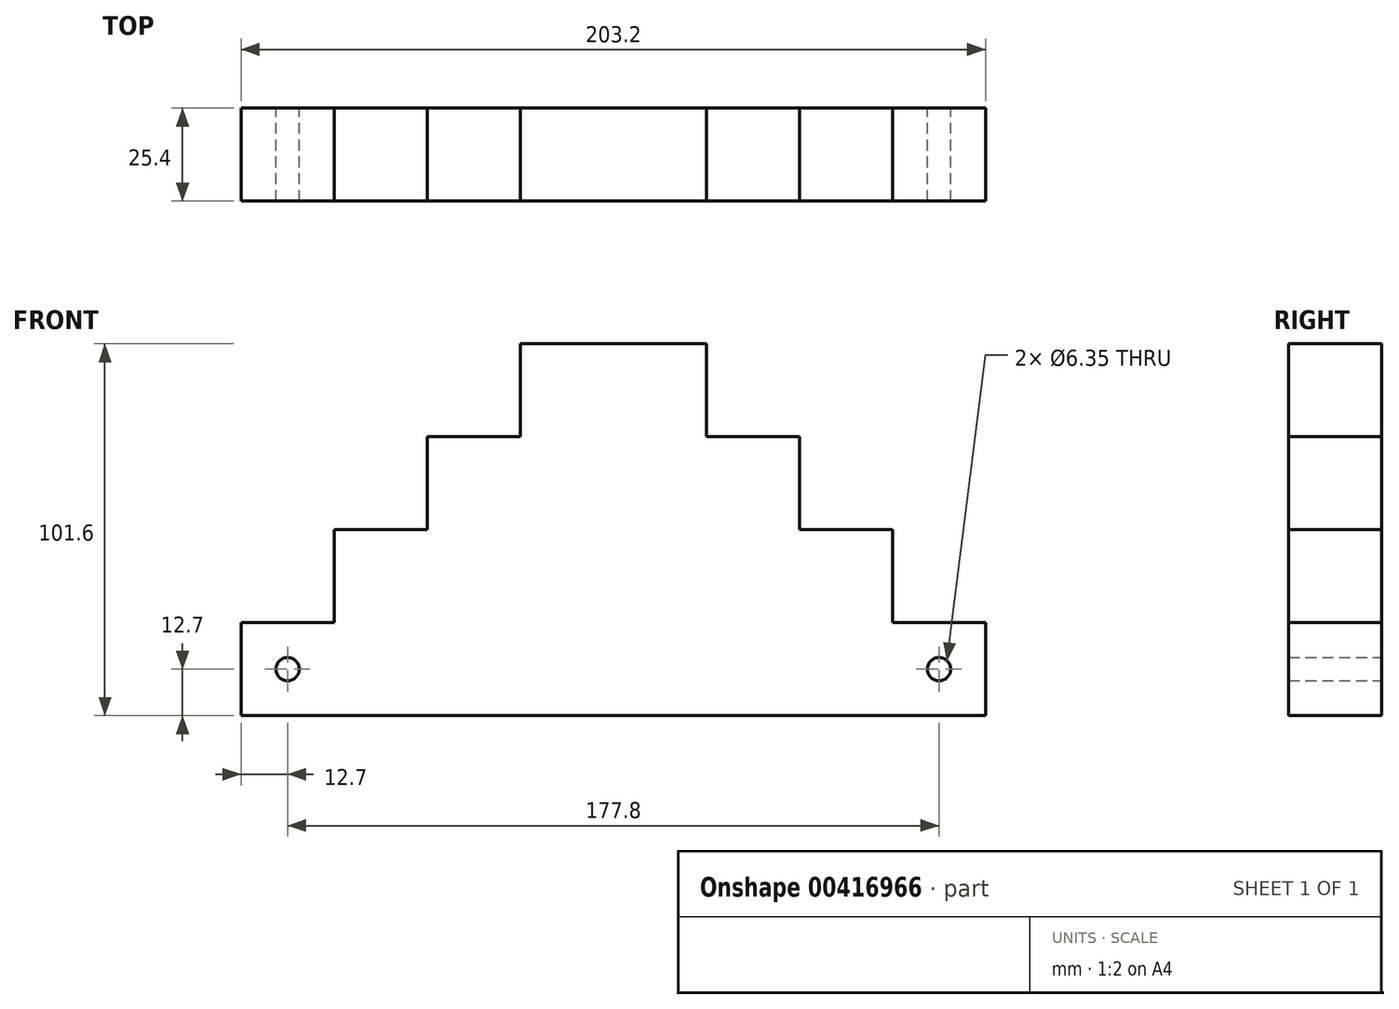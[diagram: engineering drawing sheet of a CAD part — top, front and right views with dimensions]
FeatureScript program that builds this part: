
annotation { "Feature Type Name" : "Feature", "Feature Type Description" : "" }
export const myFeature = defineFeature(function(context is Context, id is Id, definition is map)
    precondition{}
    {
        {
            var Q0;
            Q0=qCreatedBy(makeId("Front.planeOp"),FACE);
            var sketch = newSketch(context, id + "F0", { "sketchPlane" : qUnion([Q0])});
            skLineSegment(sketch, "E0", {"start": v(-353.68, 0) * mm, "end": v(351.48, 0) * mm, "construction": true});
            skLineSegment(sketch, "E1.bottom", {"start": v(0, 0) * mm, "end": v(-25.4, 0) * mm});
            skLineSegment(sketch, "E1.top", {"start": v(0, 101.6) * mm, "end": v(-25.4, 101.6) * mm});
            skLineSegment(sketch, "E1.left", {"start": v(0, 0) * mm, "end": v(0, 101.6) * mm});
            skLineSegment(sketch, "E1.right", {"start": v(-25.4, 0) * mm, "end": v(-25.4, 101.6) * mm});
            skLineSegment(sketch, "E2.bottom", {"start": v(-25.4, 76.2) * mm, "end": v(-50.8, 76.2) * mm});
            skLineSegment(sketch, "E2.top", {"start": v(-25.4, 0) * mm, "end": v(-50.8, 0) * mm});
            skLineSegment(sketch, "E2.left", {"start": v(-25.4, 76.2) * mm, "end": v(-25.4, 0) * mm});
            skLineSegment(sketch, "E2.right", {"start": v(-50.8, 76.2) * mm, "end": v(-50.8, 0) * mm});
            skLineSegment(sketch, "E3.bottom", {"start": v(-50.8, 50.8) * mm, "end": v(-76.2, 50.8) * mm});
            skLineSegment(sketch, "E3.top", {"start": v(-50.8, 0) * mm, "end": v(-76.2, 0) * mm});
            skLineSegment(sketch, "E3.left", {"start": v(-50.8, 50.8) * mm, "end": v(-50.8, 0) * mm});
            skLineSegment(sketch, "E3.right", {"start": v(-76.2, 50.8) * mm, "end": v(-76.2, 0) * mm});
            skLineSegment(sketch, "E4.bottom", {"start": v(-76.2, 25.4) * mm, "end": v(-101.6, 25.4) * mm});
            skLineSegment(sketch, "E4.top", {"start": v(-76.2, 0) * mm, "end": v(-101.6, 0) * mm});
            skLineSegment(sketch, "E4.left", {"start": v(-76.2, 25.4) * mm, "end": v(-76.2, 0) * mm});
            skLineSegment(sketch, "E4.right", {"start": v(-101.6, 25.4) * mm, "end": v(-101.6, 0) * mm});
            skLineSegment(sketch, "E5.MirrorCS", {"start": v(0, 101.6) * mm, "end": v(25.4, 101.6) * mm});
            skLineSegment(sketch, "E6.MirrorCS", {"start": v(25.4, 0) * mm, "end": v(25.4, 101.6) * mm});
            skLineSegment(sketch, "E7.MirrorCS", {"start": v(25.4, 76.2) * mm, "end": v(50.8, 76.2) * mm});
            skLineSegment(sketch, "E8.MirrorCS", {"start": v(50.8, 76.2) * mm, "end": v(50.8, 0) * mm});
            skLineSegment(sketch, "E9.MirrorCS", {"start": v(50.8, 50.8) * mm, "end": v(76.2, 50.8) * mm});
            skLineSegment(sketch, "E10.MirrorCS", {"start": v(76.2, 50.8) * mm, "end": v(76.2, 0) * mm});
            skLineSegment(sketch, "E11.MirrorCS", {"start": v(76.2, 25.4) * mm, "end": v(101.6, 25.4) * mm});
            skLineSegment(sketch, "E12.MirrorCS", {"start": v(101.6, 25.4) * mm, "end": v(101.6, 0) * mm});
            skLineSegment(sketch, "E13", {"start": v(0, 0) * mm, "end": v(101.6, 0) * mm});
            skCircle(sketch, "E14", {"center": v(-88.9, 12.7) * mm, "radius": 3.18 * mm});
            skPoint(sketch, "E14.centerSnap0", {"position": v(-88.9, 0) * mm});
            skCircle(sketch, "E15", {"center": v(88.9, 12.7) * mm, "radius": 3.18 * mm});
            skPoint(sketch, "E15.centerSnap0", {"position": v(88.9, 25.4) * mm});
            skSolve(sketch);
        }
        {
            var Q0;
            Q0 = qSketchRegion(id + "F0", true);
            extrude(context, id + "F1", {"entities" : qUnion([Q0]), "depth" : 25.4 * mm});
        }
    });
